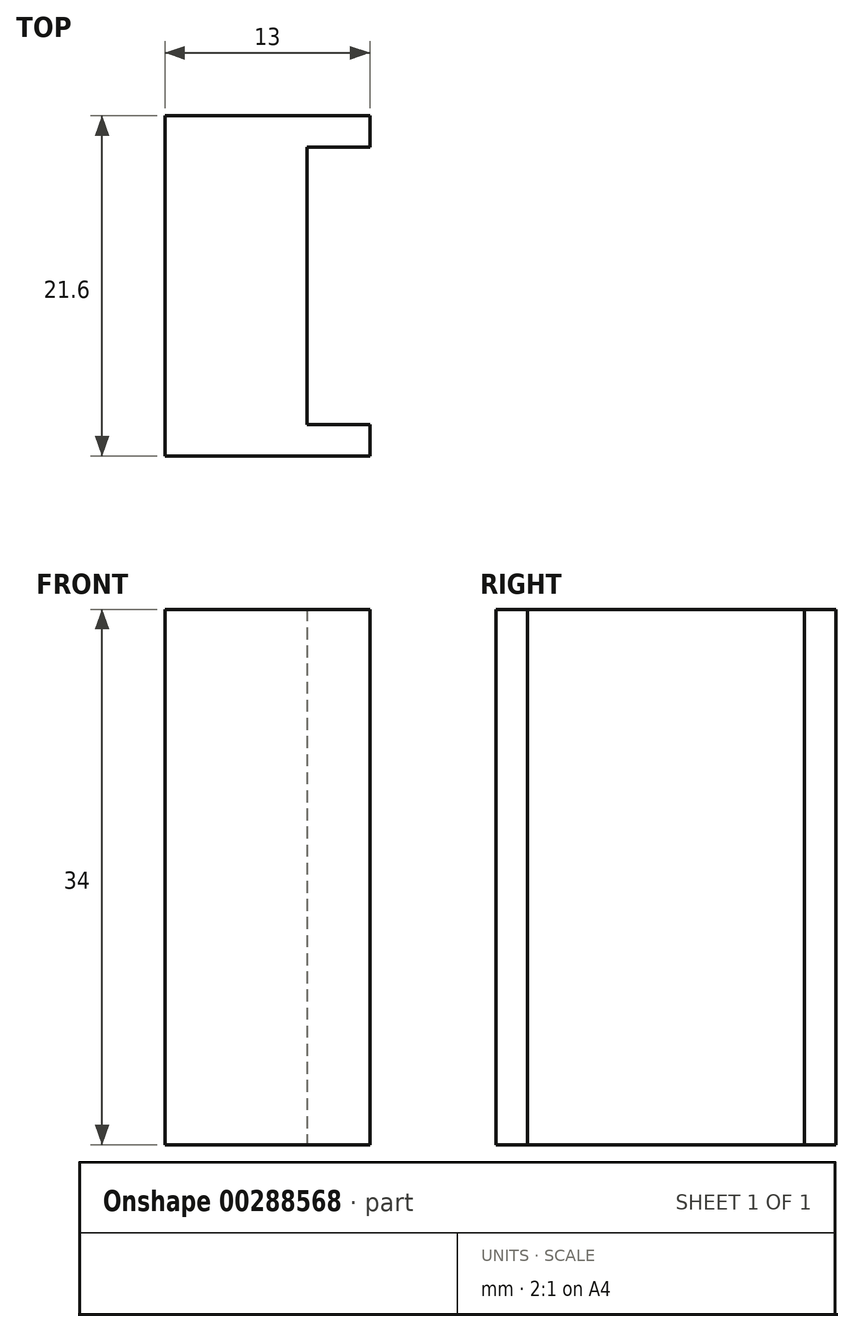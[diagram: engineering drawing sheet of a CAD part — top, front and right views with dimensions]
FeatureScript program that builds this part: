
annotation { "Feature Type Name" : "Feature", "Feature Type Description" : "" }
export const myFeature = defineFeature(function(context is Context, id is Id, definition is map)
    precondition{}
    {
        {
            var Q0;
            Q0=qCreatedBy(makeId("Top.planeOp"),FACE);
            var sketch = newSketch(context, id + "F0", { "sketchPlane" : qUnion([Q0])});
            skLineSegment(sketch, "E0.bottom", {"start": v(4.5, 10.8) * mm, "end": v(-4.5, 10.8) * mm});
            skLineSegment(sketch, "E0.top", {"start": v(4.5, -10.8) * mm, "end": v(-4.5, -10.8) * mm});
            skLineSegment(sketch, "E0.left", {"start": v(4.5, 10.8) * mm, "end": v(4.5, -10.8) * mm});
            skLineSegment(sketch, "E0.right", {"start": v(-4.5, 10.8) * mm, "end": v(-4.5, -10.8) * mm});
            skPoint(sketch, "E0.middle", {"position": v(0, 0) * mm});
            skLineSegment(sketch, "E1.bottom", {"start": v(4.5, 10.8) * mm, "end": v(8.5, 10.8) * mm});
            skLineSegment(sketch, "E1.top", {"start": v(4.5, 8.8) * mm, "end": v(8.5, 8.8) * mm});
            skLineSegment(sketch, "E1.left", {"start": v(4.5, 10.8) * mm, "end": v(4.5, 8.8) * mm});
            skLineSegment(sketch, "E1.right", {"start": v(8.5, 10.8) * mm, "end": v(8.5, 8.8) * mm});
            skLineSegment(sketch, "E2.MirrorCS", {"start": v(4.5, -8.8) * mm, "end": v(8.5, -8.8) * mm});
            skLineSegment(sketch, "E3.MirrorCS", {"start": v(4.5, -10.8) * mm, "end": v(8.5, -10.8) * mm});
            skLineSegment(sketch, "E4.MirrorCS", {"start": v(8.5, -10.8) * mm, "end": v(8.5, -8.8) * mm});
            skSolve(sketch);
        }
        {
            var Q0;
            {var subQ1=sQuery(id+"F0.wireOp",EDGE,"E0.bottom");Q0=makeQuery(id+"F0.imprint","IMPRINT",FACE,{"disambiguationData":[TD([[makeQuery(id+"F0.imprint","IMPRINT",EDGE,{"derivedFrom":subQ1}),1.0]])]});}
            var Q1;
            {var subQ0=sQuery(id+"F0.wireOp",EDGE,"E1.bottom");Q1=makeQuery(id+"F0.imprint","IMPRINT",FACE,{"disambiguationData":[TD([[makeQuery(id+"F0.imprint","IMPRINT",EDGE,{"derivedFrom":subQ0}),-1.0]])]});}
            var Q2;
            {var subQ2=sQuery(id+"F0.wireOp",EDGE,"E2.MirrorCS");Q2=makeQuery(id+"F0.imprint","IMPRINT",FACE,{"disambiguationData":[TD([[makeQuery(id+"F0.imprint","IMPRINT",EDGE,{"derivedFrom":subQ2}),-1.0]])]});}
            extrude(context, id + "F1", {"entities" : qUnion([Q0, Q1, Q2]), "depth" : 34 * mm, "offsetDistance" : 25 * mm});
        }
    });
